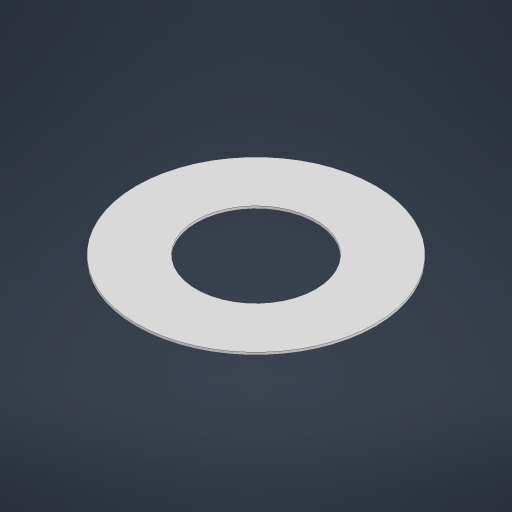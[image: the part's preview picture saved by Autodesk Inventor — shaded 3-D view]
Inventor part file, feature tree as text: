
AUTODESK INVENTOR PART (.ipt)
format: ipt  version: 2024 (Build 280153000, 153)  size: 405,504 bytes
history: native  units: mm
features: other x1, extrude x1, sketch x1
ambient origin geometry x8: Origin, YZ Plane, XZ Plane, XY Plane, X Axis, Y Axis, Z Axis, Center Point
bodies: Body1 (feature_tree)
feature tree (3):
  other  "솔리드1"
  extrude  "돌출1"  Depth=10.0mm
  sketch  "스케치1"
